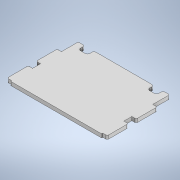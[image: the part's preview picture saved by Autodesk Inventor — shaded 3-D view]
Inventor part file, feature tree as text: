
AUTODESK INVENTOR PART (.ipt)
format: ipt  version: 2020 (Build 240168000, 168)  size: 180,736 bytes
history: native  units: mm
features: extrude x1, sketch x1
ambient origin geometry x8: Origin, YZ Plane, XZ Plane, XY Plane, X Axis, Y Axis, Z Axis, Center Point
bodies: Solid1 (feature_tree)
feature tree (2):
  extrude  "Extrusion1"  Depth=2.0mm
  sketch  "Sketch1"  dims[d3=6.0mm d8=2.0mm d11=2.0mm d12=2.0mm d13=9.0mm d14=83.0mm d15=12.7mm d16=12.7mm d17=2.0mm d18=3.0mm d19=3.0mm d23=94.00005mm d24=6.0mm d25=1.0mm d26=1.0mm d27=5.0mm d28=0.0mm d29=29.0mm d30=23.325mm d31=2.0mm d32=69.0mm d33=11.0mm d34=2.0mm d35=126.5mm]
